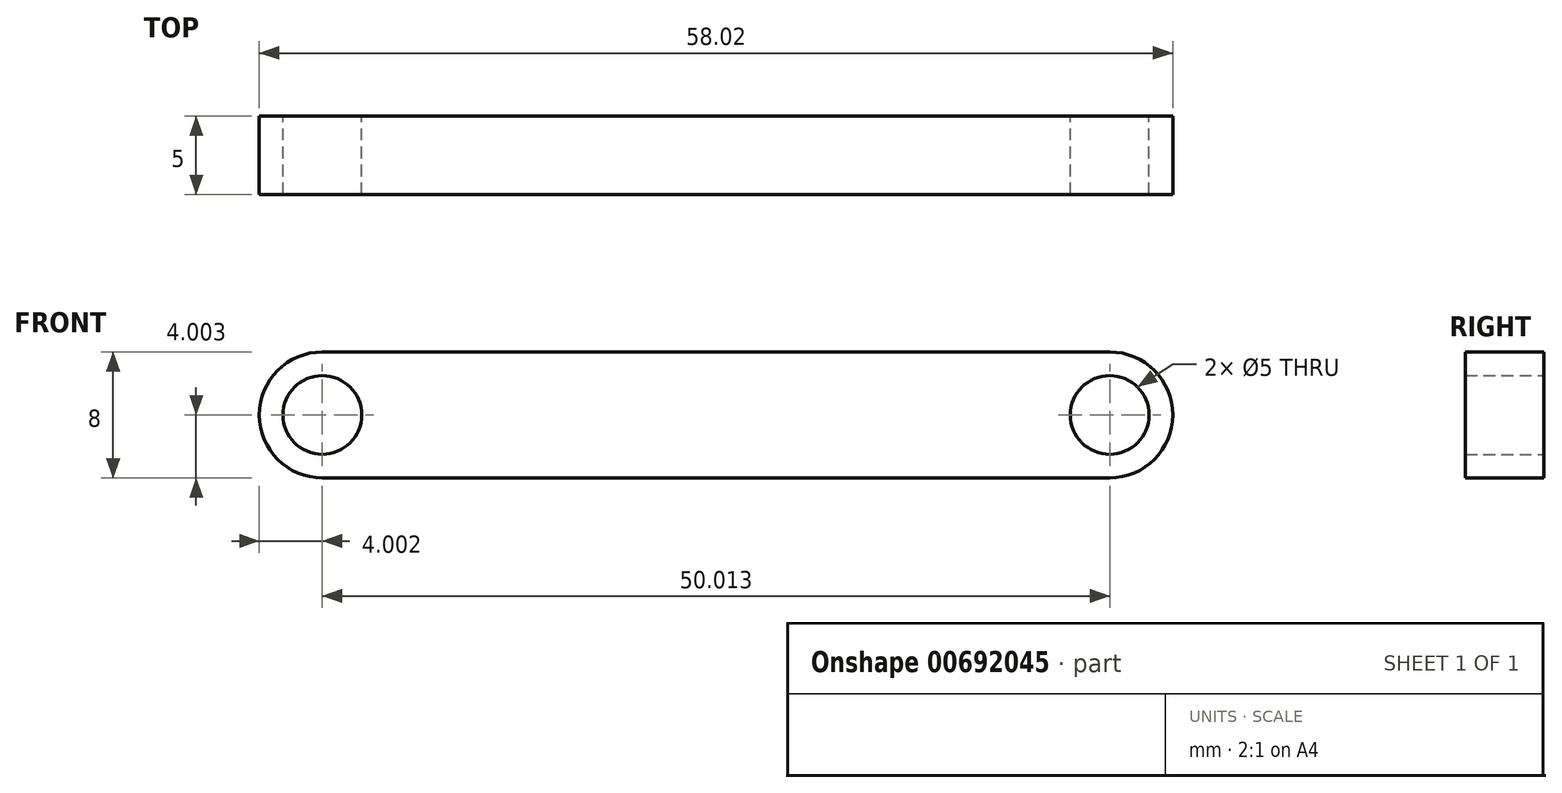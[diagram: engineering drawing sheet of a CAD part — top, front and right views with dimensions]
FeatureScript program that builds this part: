
annotation { "Feature Type Name" : "Feature", "Feature Type Description" : "" }
export const myFeature = defineFeature(function(context is Context, id is Id, definition is map)
    precondition{}
    {
        {
            var Q0;
            Q0=qCreatedBy(makeId("Front.planeOp"),FACE);
            var sketch = newSketch(context, id + "F0", { "sketchPlane" : qUnion([Q0])});
            skLineSegment(sketch, "E0.bottom", {"start": v(-19.08, 3) * mm, "end": v(30.93, 3) * mm});
            skLineSegment(sketch, "E0.top", {"start": v(-19.08, -5) * mm, "end": v(30.93, -5) * mm});
            skArc(sketch, "E1", {"start": v(-19.08, 3) * mm, "mid": v(-23.08, -1) * mm, "end": v(-19.08, -5) * mm});
            skArc(sketch, "E2", {"start": v(30.93, -5) * mm, "mid": v(34.94, -1) * mm, "end": v(30.93, 3) * mm});
            skCircle(sketch, "E3", {"center": v(-19.08, -1) * mm, "radius": 2.5 * mm});
            skCircle(sketch, "E4", {"center": v(30.93, -1) * mm, "radius": 2.5 * mm});
            skSolve(sketch);
        }
        {
            var Q0;
            Q0=makeQuery(id+"F0.imprint","IMPRINT",FACE,{"disambiguationData":[TD([[makeQuery(id+"F0.imprint","IMPRINT",EDGE,{"derivedFrom":sQuery(id+"F0.wireOp",EDGE,"E0.bottom")}),-1.0]])]});
            extrude(context, id + "F1", {"entities" : qUnion([Q0]), "depth" : 5 * mm, "offsetDistance" : 25 * mm});
        }
    });
